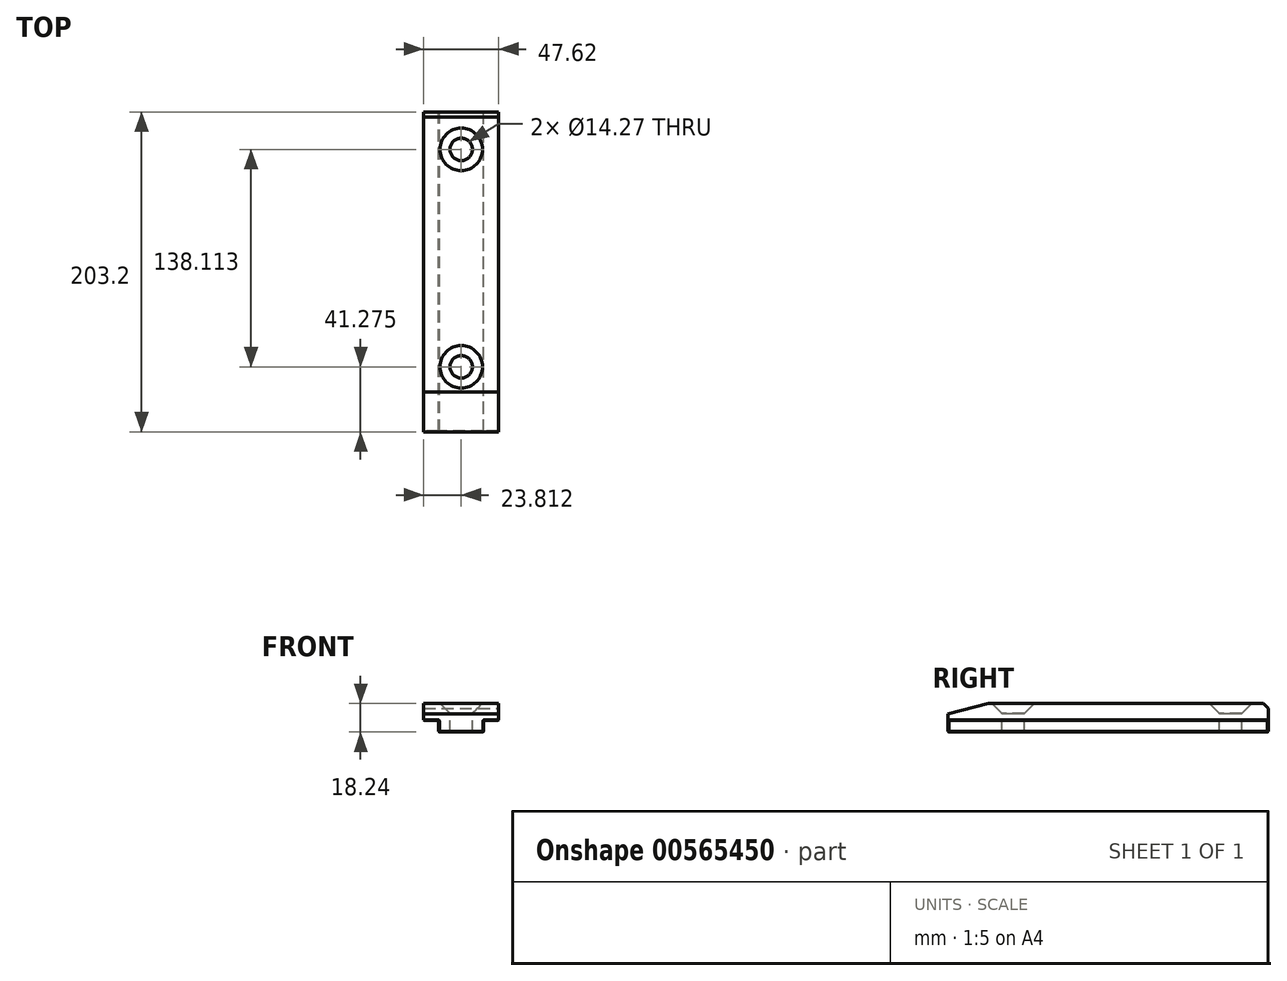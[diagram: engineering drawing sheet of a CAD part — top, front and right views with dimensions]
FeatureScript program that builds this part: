
annotation { "Feature Type Name" : "Feature", "Feature Type Description" : "" }
export const myFeature = defineFeature(function(context is Context, id is Id, definition is map)
    precondition{}
    {
        {
            var Q0;
            Q0=qCreatedBy(makeId("Front.planeOp"),FACE);
            var sketch = newSketch(context, id + "F0", { "sketchPlane" : qUnion([Q0])});
            skLineSegment(sketch, "E0", {"start": v(0, 0) * mm, "end": v(47.63, 0) * mm});
            skLineSegment(sketch, "E1", {"start": v(0, 0) * mm, "end": v(0, -10.87) * mm});
            skLineSegment(sketch, "E2.left", {"start": v(47.63, 0) * mm, "end": v(47.63, -10.87) * mm});
            skLineSegment(sketch, "E2.right", {"start": v(47.62, 0) * mm, "end": v(47.62, -10.87) * mm});
            skLineSegment(sketch, "E3", {"start": v(9.53, -18.24) * mm, "end": v(38.1, -18.24) * mm});
            skLineSegment(sketch, "E4", {"start": v(9.53, -18.24) * mm, "end": v(9.53, -10.87) * mm});
            skLineSegment(sketch, "E5", {"start": v(38.1, -18.24) * mm, "end": v(38.1, -10.87) * mm});
            skLineSegment(sketch, "E6", {"start": v(9.53, -10.87) * mm, "end": v(0, -10.87) * mm});
            skLineSegment(sketch, "E7", {"start": v(38.1, -10.87) * mm, "end": v(47.63, -10.87) * mm});
            skSolve(sketch);
        }
        {
            var Q0;
            Q0 = qSketchRegion(id + "F0", true);
            extrude(context, id + "F1", {"entities" : qUnion([Q0]), "depth" : 203.2 * mm, "offsetDistance" : 25.4 * mm});
        }
        {
            var Q0;
            Q0=makeQuery(id+"F1.opExtrude","SWEPT_FACE",FACE,{"disambiguationData":[OSD([sQuery(id+"F0.wireOp",EDGE,"E1")])]});
            var sketch = newSketch(context, id + "F2", { "sketchPlane" : qUnion([Q0])});
            skLineSegment(sketch, "E8", {"start": v(203.2, 0) * mm, "end": v(177.8, 0) * mm});
            skLineSegment(sketch, "E9", {"start": v(177.8, 0) * mm, "end": v(203.2, -6.8) * mm});
            skLineSegment(sketch, "E10", {"start": v(203.2, 0) * mm, "end": v(203.2, -6.8) * mm});
            skSolve(sketch);
        }
        {
            var Q0;
            Q0 = qSketchRegion(id + "F2", true);
            extrude(context, id + "F3", {"entities" : qUnion([Q0]), "operationType" : NewBodyOperationType.REMOVE, "endBound" : BoundingType.THROUGH_ALL, "oppositeDirection" : true, "depth" : 25.4 * mm, "offsetDistance" : 25.4 * mm});
        }
        {
            var Q0;
            Q0=makeQuery(id+"F1.opExtrude","SWEPT_FACE",FACE,{"disambiguationData":[OSD([sQuery(id+"F0.wireOp",EDGE,"E0")])]});
            var sketch = newSketch(context, id + "F4", { "sketchPlane" : qUnion([Q0])});
            skPoint(sketch, "E11", {"position": v(23.81, -23.81) * mm});
            skPoint(sketch, "E12", {"position": v(23.81, -161.93) * mm});
            skSolve(sketch);
        }
        {
            var Q0;
            Q0=sQuery(id+"F4.wireOp",VERTEX,"E11");
            var Q1;
            Q1=sQuery(id+"F4.wireOp",VERTEX,"E12");
            var Q2;
            Q2=makeQuery(id+"F1.opExtrude","SWEPT_BODY",BODY,{"disambiguationData":[OSD([sQuery(id+"F0.wireOp",EDGE,"E0"),sQuery(id+"F0.wireOp",EDGE,"E1"),sQuery(id+"F0.wireOp",EDGE,"E2.right"),sQuery(id+"F0.wireOp",EDGE,"E3"),sQuery(id+"F0.wireOp",EDGE,"E4"),sQuery(id+"F0.wireOp",EDGE,"E5"),sQuery(id+"F0.wireOp",EDGE,"E6"),sQuery(id+"F0.wireOp",EDGE,"E7")])]});
            hole(context, id + "F5", {"style" : HoleStyle.C_SINK, "endStyle" : HoleEndStyle.THROUGH, "holeDiameter" : 14.27 * mm, "cSinkDiameter" : 26.97 * mm, "cSinkAngle" : 90 * degree, "isTappedThrough" : true, "tappedDepth" : 1.27 * mm, "tapClearance" : 3, "startFromSketch" : true, "locations" : qUnion([Q0, Q1]), "scope" : qUnion([Q2])});
        }
        {
            var Q0;
            Q0=makeQuery(id+"F1.opExtrude","CAP_EDGE",EDGE,{"disambiguationData":[OSD([sQuery(id+"F0.wireOp",EDGE,"E0")])],"isStart":true});
            chamfer(context, id + "F6", {"entities" : qUnion([Q0]), "width" : 3.17 * mm, "tangentPropagation" : true});
        }
        {
            var Q0;
            Q0=makeQuery(id+"F1.opExtrude","SWEPT_EDGE",EDGE,{"disambiguationData":[OSD([sQuery(id+"F0.wireOp",EDGE,"E4"),sQuery(id+"F0.wireOp",EDGE,"E6")])]});
            var Q1;
            Q1=makeQuery(id+"F1.opExtrude","SWEPT_EDGE",EDGE,{"disambiguationData":[OSD([sQuery(id+"F0.wireOp",EDGE,"E5"),sQuery(id+"F0.wireOp",EDGE,"E7")])]});
            fillet(context, id + "F7", {"entities" : qUnion([Q0, Q1]), "radius" : 0.25 * mm, "tangentPropagation" : true, "allowEdgeOverflow" : false});
        }
        {
            var Q0;
            Q0=makeQuery(id+"F1.opExtrude","SWEPT_EDGE",EDGE,{"disambiguationData":[OSD([sQuery(id+"F0.wireOp",EDGE,"E3"),sQuery(id+"F0.wireOp",EDGE,"E5")])]});
            var Q1;
            Q1=makeQuery(id+"F1.opExtrude","SWEPT_EDGE",EDGE,{"disambiguationData":[OSD([sQuery(id+"F0.wireOp",EDGE,"E3"),sQuery(id+"F0.wireOp",EDGE,"E4")])]});
            var Q2;
            Q2=makeQuery(id+"F1.opExtrude","CAP_EDGE",EDGE,{"disambiguationData":[OSD([sQuery(id+"F0.wireOp",EDGE,"E3")])],"isStart":false});
            var Q3;
            Q3=makeQuery(id+"F1.opExtrude","CAP_EDGE",EDGE,{"disambiguationData":[OSD([sQuery(id+"F0.wireOp",EDGE,"E3")])],"isStart":true});
            var Q4;
            Q4=makeQuery(id+"F1.opExtrude","CAP_EDGE",EDGE,{"disambiguationData":[OSD([sQuery(id+"F0.wireOp",EDGE,"E5")])],"isStart":true});
            var Q5;
            Q5=makeQuery(id+"F1.opExtrude","CAP_EDGE",EDGE,{"disambiguationData":[OSD([sQuery(id+"F0.wireOp",EDGE,"E4")])],"isStart":true});
            var Q6;
            Q6=makeQuery(id+"F1.opExtrude","CAP_EDGE",EDGE,{"disambiguationData":[OSD([sQuery(id+"F0.wireOp",EDGE,"E4")])],"isStart":false});
            var Q7;
            Q7=makeQuery(id+"F1.opExtrude","CAP_EDGE",EDGE,{"disambiguationData":[OSD([sQuery(id+"F0.wireOp",EDGE,"E5")])],"isStart":false});
            var Q8;
            Q8=makeQuery(id+"F1.opExtrude","SWEPT_EDGE",EDGE,{"disambiguationData":[OSD([sQuery(id+"F0.wireOp",EDGE,"E2.right"),sQuery(id+"F0.wireOp",EDGE,"E7")])]});
            var Q9;
            Q9=makeQuery(id+"F1.opExtrude","SWEPT_EDGE",EDGE,{"disambiguationData":[OSD([sQuery(id+"F0.wireOp",EDGE,"E1"),sQuery(id+"F0.wireOp",EDGE,"E6")])]});
            chamfer(context, id + "F8", {"entities" : qUnion([Q0, Q1, Q2, Q3, Q4, Q5, Q6, Q7, Q8, Q9]), "width" : 0.38 * mm, "tangentPropagation" : true});
        }
    });
